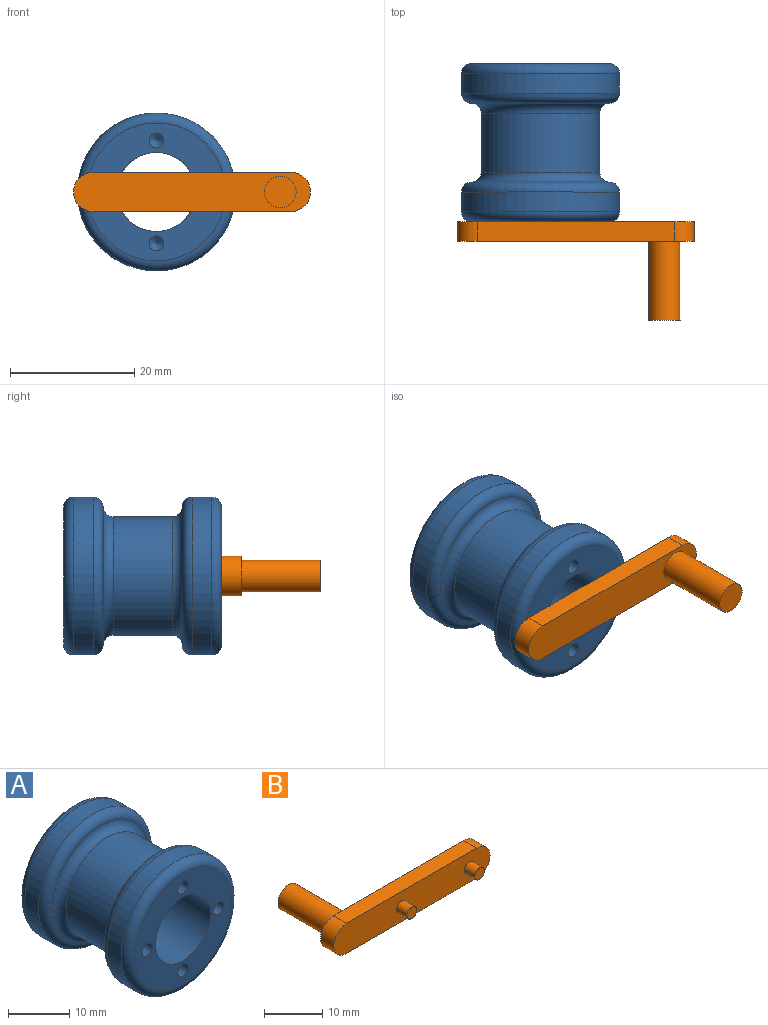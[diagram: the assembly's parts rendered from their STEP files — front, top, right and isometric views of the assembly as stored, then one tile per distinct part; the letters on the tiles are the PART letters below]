
ASSEMBLY  parts=2 mates=1
PART A: 20 faces, bbox 27.5x25.4x27.5 mm
  f0: cylinder r=12.7mm len=25.4mm, axis (0,1,0), area 251.3mm2, adj f16,f17
  f1: plane 22.2x22.2mm, normal (0,1,0), area 260.4mm2, adj f5,f16
  f2: cylinder r=9.53mm len=19.05mm, axis (0,1,0), area 568.5mm2, adj f18,f19
  f3: cylinder r=12.7mm len=25.4mm, axis (0,1,0), area 251.3mm2, adj f14,f15
  f4: plane 22.2x22.2mm, normal (0,-1,0), area 242.5mm2, adj f5,f6,f8,f10,f12,f15
  f5: cylinder r=6.35mm len=25.4mm, axis (0,-1,0), area 1013.4mm2, adj f1,f4
  f6: cylinder r=1.19mm len=3.18mm, axis (0,-1,0), area 23.8mm2, adj f4,f7
  f7: cone r=0mm half-angle=59deg, axis (0,-1,0), area 5.2mm2, adj f6
  f8: cylinder r=1.19mm len=3.18mm, axis (0,-1,0), area 23.8mm2, adj f4,f9
  f9: cone r=0mm half-angle=59deg, axis (0,-1,0), area 5.2mm2, adj f8
  f10: cylinder r=1.19mm len=3.18mm, axis (0,-1,0), area 23.8mm2, adj f4,f11
  f11: cone r=0mm half-angle=59deg, axis (0,-1,0), area 5.2mm2, adj f10
  f12: cylinder r=1.19mm len=3.18mm, axis (0,-1,0), area 23.8mm2, adj f4,f13
  f13: cone r=0mm half-angle=59deg, axis (0,-1,0), area 5.2mm2, adj f12
  f14: torus R=11.1mm, axis (0,-1,0), area 190.5mm2, adj f3,f19
  f15: torus R=11.1mm, axis (0,-1,0), area 191.4mm2, adj f3,f4
  f16: torus R=11.1mm, axis (0,-1,0), area 191.4mm2, adj f0,f1
  f17: torus R=11.1mm, axis (0,-1,0), area 190.5mm2, adj f0,f18
  f18: torus R=11.13mm, axis (0,-1,0), area 158.7mm2, adj f2,f17
  f19: torus R=11.13mm, axis (0,-1,0), area 158.7mm2, adj f2,f14
PART B: 12 faces, bbox 38.1x18.4x6.4 mm
  f0: plane 31.75x3.18mm, normal (0,0,1), area 100.8mm2, adj f1,f3,f4,f5
  f1: cylinder r=3.17mm len=6.35mm, axis (0,1,0), area 31.7mm2, adj f0,f2,f4,f5
  f2: plane 31.75x3.18mm, normal (0,0,-1), area 100.8mm2, adj f1,f3,f4,f5
  f3: cylinder r=3.17mm len=6.35mm, axis (0,1,0), area 31.7mm2, adj f0,f2,f4,f5
  f4: plane 38.1x6.35mm, normal (0,-1,0), area 224.3mm2, adj f0,f1,f2,f3,f8,f10
  f5: plane 38.1x6.35mm, normal (0,1,0), area 213mm2, adj f0,f1,f2,f3,f6
  f6: cylinder r=2.54mm len=12.7mm, axis (0,-1,0), area 202.7mm2, adj f5,f7
  f7: plane 5.08x5.08mm, normal (0,1,0), area 20.3mm2, adj f6
  f8: cylinder r=1.19mm len=2.54mm, axis (0,1,0), area 19.1mm2, adj f4,f9
  f9: plane 2.39x2.39mm, normal (0,-1,0), area 4.5mm2, adj f8
  f10: cylinder r=1.19mm len=2.54mm, axis (0,1,0), area 19.1mm2, adj f4,f11
  f11: plane 2.39x2.39mm, normal (0,-1,0), area 4.5mm2, adj f10
PLACE A t=(-13.74,3.83,-1.4)mm
PLACE B rot(axis=(0,0,1),180deg) t=(11.02,-24.74,-4.57)mm
MATE fastened B.f8 <-> A.f12  axis (0,1,0) through (-5.49,-21.57,-1.4)mm
